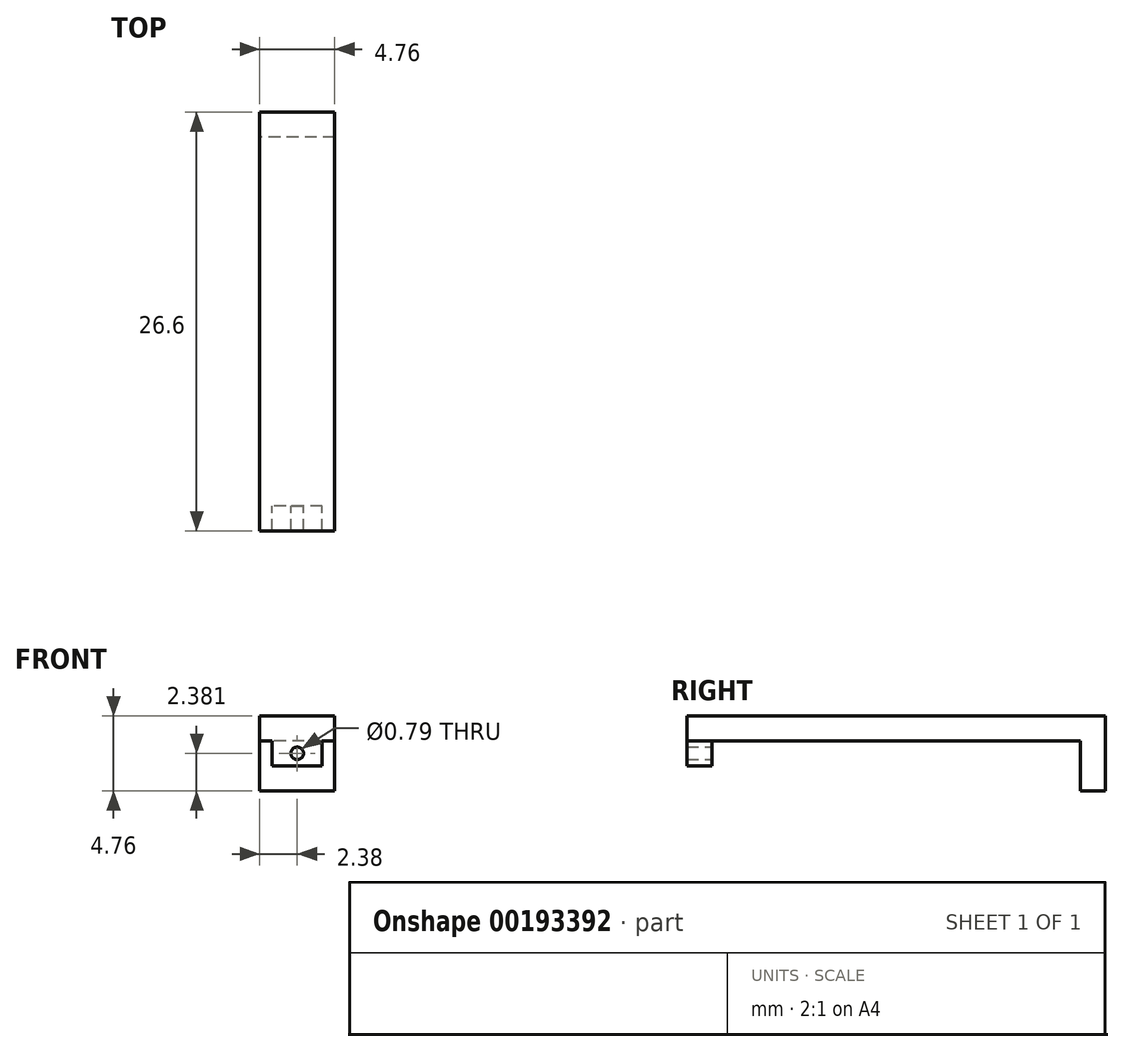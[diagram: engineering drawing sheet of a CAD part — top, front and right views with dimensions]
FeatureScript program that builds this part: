
annotation { "Feature Type Name" : "Feature", "Feature Type Description" : "" }
export const myFeature = defineFeature(function(context is Context, id is Id, definition is map)
    precondition{}
    {
        {
            var Q0;
            Q0=qCreatedBy(makeId("Top.planeOp"),FACE);
            var sketch = newSketch(context, id + "F0", { "sketchPlane" : qUnion([Q0])});
            skLineSegment(sketch, "E0.bottom", {"start": v(2.38, 13.3) * mm, "end": v(-2.38, 13.3) * mm});
            skLineSegment(sketch, "E0.top", {"start": v(2.38, -13.3) * mm, "end": v(-2.38, -13.3) * mm});
            skLineSegment(sketch, "E0.left", {"start": v(2.38, 13.3) * mm, "end": v(2.38, -13.3) * mm});
            skLineSegment(sketch, "E0.right", {"start": v(-2.38, 13.3) * mm, "end": v(-2.38, -13.3) * mm});
            skPoint(sketch, "E0.middle", {"position": v(0, 0) * mm});
            skSolve(sketch);
        }
        {
            var Q0;
            Q0 = qSketchRegion(id + "F0", true);
            extrude(context, id + "F1", {"entities" : qUnion([Q0]), "depth" : 4.76 * mm});
        }
        {
            var Q0;
            Q0=makeQuery(id+"F1.opExtrude","CAP_FACE",FACE,{"disambiguationData":[OSD([sQuery(id+"F0.wireOp",EDGE,"E0.bottom"),sQuery(id+"F0.wireOp",EDGE,"E0.top"),sQuery(id+"F0.wireOp",EDGE,"E0.left"),sQuery(id+"F0.wireOp",EDGE,"E0.right")])],"isStart":true});
            var sketch = newSketch(context, id + "F2", { "sketchPlane" : qUnion([Q0])});
            skLineSegment(sketch, "E1.bottom", {"start": v(2.38, -11.7) * mm, "end": v(-2.38, -11.7) * mm});
            skLineSegment(sketch, "E1.top", {"start": v(2.38, 13.3) * mm, "end": v(1.59, 13.3) * mm});
            skLineSegment(sketch, "E1.left", {"start": v(2.38, -11.7) * mm, "end": v(2.38, 13.3) * mm});
            skLineSegment(sketch, "E1.right", {"start": v(-2.38, -11.7) * mm, "end": v(-2.38, 13.3) * mm});
            skLineSegment(sketch, "E2.top", {"start": v(1.59, 11.7) * mm, "end": v(-1.59, 11.7) * mm});
            skLineSegment(sketch, "E2.left", {"start": v(1.59, 13.3) * mm, "end": v(1.59, 11.7) * mm});
            skLineSegment(sketch, "E2.right", {"start": v(-1.59, 13.3) * mm, "end": v(-1.59, 11.7) * mm});
            skLineSegment(sketch, "E3.trimOffspring", {"start": v(-1.59, 13.3) * mm, "end": v(-2.38, 13.3) * mm});
            skSolve(sketch);
        }
        {
            var Q0;
            Q0 = qSketchRegion(id + "F2", true);
            extrude(context, id + "F3", {"entities" : qUnion([Q0]), "operationType" : NewBodyOperationType.REMOVE, "oppositeDirection" : true, "depth" : 3.17 * mm});
        }
        {
            var Q0;
            {var subQ0=sQuery(id+"F0.wireOp",EDGE,"E0.top");Q0=makeQuery(id+"F3.boolean.opBoolean","SPLIT",FACE,{"disambiguationData":[TD([makeQuery(id+"F1.opExtrude","SWEPT_FACE",FACE,{"disambiguationData":[OSD([subQ0])]})])],"derivedFrom":makeQuery(id+"F1.opExtrude","CAP_FACE",FACE,{"disambiguationData":[OSD([sQuery(id+"F0.wireOp",EDGE,"E0.bottom"),subQ0,sQuery(id+"F0.wireOp",EDGE,"E0.left"),sQuery(id+"F0.wireOp",EDGE,"E0.right")])],"isStart":true})});}
            extrude(context, id + "F4", {"entities" : qUnion([Q0]), "operationType" : NewBodyOperationType.REMOVE, "oppositeDirection" : true, "depth" : 1.59 * mm});
        }
        {
            var Q0;
            Q0=makeQuery(id+"F3.boolean.opBoolean","COPY",FACE,{"derivedFrom":makeQuery(id+"F3.opExtrude","SWEPT_FACE",FACE,{"disambiguationData":[OSD([sQuery(id+"F2.wireOp",EDGE,"E2.top")])]})});
            var sketch = newSketch(context, id + "F5", { "sketchPlane" : qUnion([Q0])});
            skCircle(sketch, "E4", {"center": v(0, 2.38) * mm, "radius": 0.4 * mm});
            skPoint(sketch, "E4.centerSnap0", {"position": v(0, 1.59) * mm});
            skPoint(sketch, "E4.centerSnap1", {"position": v(-1.59, 2.38) * mm});
            skSolve(sketch);
        }
        {
            var Q0;
            Q0 = qSketchRegion(id + "F5", true);
            extrude(context, id + "F6", {"entities" : qUnion([Q0]), "operationType" : NewBodyOperationType.REMOVE, "endBound" : BoundingType.THROUGH_ALL, "oppositeDirection" : true, "depth" : 25.4 * mm});
        }
    });
